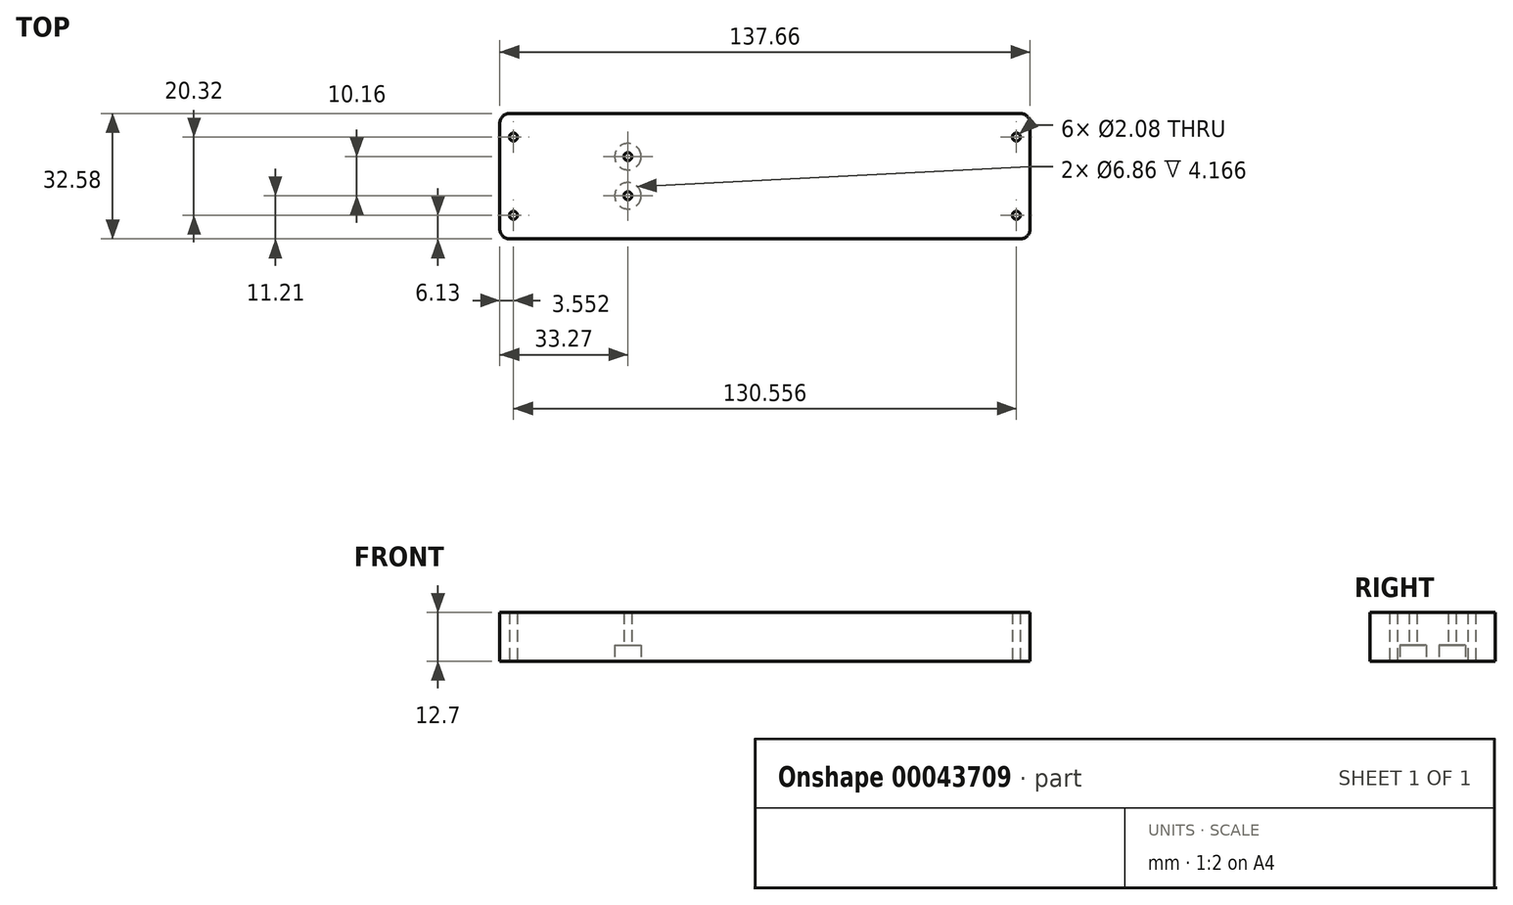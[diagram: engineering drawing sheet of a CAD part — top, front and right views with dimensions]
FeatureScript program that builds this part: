
annotation { "Feature Type Name" : "Feature", "Feature Type Description" : "" }
export const myFeature = defineFeature(function(context is Context, id is Id, definition is map)
    precondition{}
    {
        {
            var Q0;
            Q0=qCreatedBy(makeId("Top.planeOp"),FACE);
            var sketch = newSketch(context, id + "F0", { "sketchPlane" : qUnion([Q0])});
            skLineSegment(sketch, "E0.rect.bottom", {"start": v(-66.3, -16.3) * mm, "end": v(66.3, -16.3) * mm});
            skLineSegment(sketch, "E0.rect.top", {"start": v(-66.3, 16.3) * mm, "end": v(66.3, 16.3) * mm});
            skLineSegment(sketch, "E0.rect.left", {"start": v(-68.83, -13.75) * mm, "end": v(-68.83, 13.75) * mm});
            skLineSegment(sketch, "E0.rect.right", {"start": v(68.83, -13.75) * mm, "end": v(68.83, 13.75) * mm});
            skPoint(sketch, "E0.rect.middle", {"position": v(0, 0) * mm});
            skLineSegment(sketch, "E1", {"start": v(0, 16.3) * mm, "end": v(0, -16.3) * mm, "construction": true});
            skLineSegment(sketch, "E2", {"start": v(-68.83, 0) * mm, "end": v(68.83, 0) * mm, "construction": true});
            skLineSegment(sketch, "E3.rect.bottom", {"start": v(-65.28, -10.16) * mm, "end": v(65.28, -10.16) * mm, "construction": true});
            skLineSegment(sketch, "E3.rect.top", {"start": v(-65.28, 10.16) * mm, "end": v(65.28, 10.16) * mm, "construction": true});
            skLineSegment(sketch, "E3.rect.left", {"start": v(-65.28, -10.16) * mm, "end": v(-65.28, 10.16) * mm, "construction": true});
            skLineSegment(sketch, "E3.rect.right", {"start": v(65.28, -10.16) * mm, "end": v(65.28, 10.16) * mm, "construction": true});
            skCircle(sketch, "E4", {"center": v(-65.28, 10.16) * mm, "radius": 1.04 * mm});
            skCircle(sketch, "E5", {"center": v(-65.28, -10.16) * mm, "radius": 1.04 * mm});
            skCircle(sketch, "E6", {"center": v(65.28, 10.16) * mm, "radius": 1.04 * mm});
            skCircle(sketch, "E7", {"center": v(65.28, -10.16) * mm, "radius": 1.04 * mm});
            skPoint(sketch, "E8.visualSharp", {"position": v(-68.83, 16.3) * mm});
            skArc(sketch, "E8.filletArc", {"start": v(-66.3, 16.3) * mm, "mid": v(-68.1, 15.55) * mm, "end": v(-68.83, 13.75) * mm});
            skPoint(sketch, "E9.visualSharp", {"position": v(-68.83, -16.3) * mm});
            skArc(sketch, "E9.filletArc", {"start": v(-68.83, -13.75) * mm, "mid": v(-68.1, -15.55) * mm, "end": v(-66.3, -16.3) * mm});
            skPoint(sketch, "E10.visualSharp", {"position": v(68.83, 16.3) * mm});
            skArc(sketch, "E10.filletArc", {"start": v(68.83, 13.75) * mm, "mid": v(68.1, 15.55) * mm, "end": v(66.3, 16.3) * mm});
            skPoint(sketch, "E11.visualSharp", {"position": v(68.83, -16.3) * mm});
            skArc(sketch, "E11.filletArc", {"start": v(66.3, -16.3) * mm, "mid": v(68.1, -15.55) * mm, "end": v(68.83, -13.75) * mm});
            skLineSegment(sketch, "E12", {"start": v(-35.56, 16.3) * mm, "end": v(-35.56, -16.3) * mm, "construction": true});
            skSolve(sketch);
        }
        {
            var Q0;
            Q0=makeQuery(id+"F0.imprint","IMPRINT",FACE,{"disambiguationData":[TD([[makeQuery(id+"F0.imprint","IMPRINT",EDGE,{"derivedFrom":sQuery(id+"F0.wireOp",EDGE,"E0.rect.left")}),-1.0]])]});
            var Q1;
            Q1=makeQuery(id+"F0.imprint","IMPRINT",FACE,{"disambiguationData":[TD([[makeQuery(id+"F0.imprint","IMPRINT",EDGE,{"derivedFrom":sQuery(id+"F0.wireOp",EDGE,"E0.rect.right")}),1.0]])]});
            extrude(context, id + "F1", {"entities" : qUnion([Q0, Q1]), "depth" : 12.7 * mm});
        }
        {
            var Q0;
            Q0=makeQuery(id+"F1.opExtrude","CAP_FACE",FACE,{"disambiguationData":[OSD([sQuery(id+"F0.wireOp",EDGE,"E0.rect.bottom"),sQuery(id+"F0.wireOp",EDGE,"E0.rect.top"),sQuery(id+"F0.wireOp",EDGE,"E0.rect.left"),sQuery(id+"F0.wireOp",EDGE,"E0.rect.right"),sQuery(id+"F0.wireOp",EDGE,"E4"),sQuery(id+"F0.wireOp",EDGE,"E5"),sQuery(id+"F0.wireOp",EDGE,"E6"),sQuery(id+"F0.wireOp",EDGE,"E7"),sQuery(id+"F0.wireOp",EDGE,"E8.filletArc"),sQuery(id+"F0.wireOp",EDGE,"E9.filletArc"),sQuery(id+"F0.wireOp",EDGE,"E10.filletArc"),sQuery(id+"F0.wireOp",EDGE,"E11.filletArc")])],"isStart":true});
            var sketch = newSketch(context, id + "F2", { "sketchPlane" : qUnion([Q0])});
            skLineSegment(sketch, "E13", {"start": v(-68.83, 0) * mm, "end": v(0, 0) * mm, "construction": true});
            skLineSegment(sketch, "E14", {"start": v(0, 16.3) * mm, "end": v(0, -16.3) * mm, "construction": true});
            skCircle(sketch, "E15", {"center": v(-35.56, 5.08) * mm, "radius": 1.04 * mm});
            skCircle(sketch, "E16.MirrorC", {"center": v(-35.56, -5.08) * mm, "radius": 1.04 * mm});
            skSolve(sketch);
        }
        {
            var Q0;
            Q0=sQuery(id+"F2.wireOp",VERTEX,"E15.center");
            var Q1;
            Q1=sQuery(id+"F2.wireOp",VERTEX,"E16.MirrorC.center");
            var Q2;
            Q2=makeQuery(id+"F1.opExtrude","SWEPT_BODY",BODY,{"disambiguationData":[OSD([sQuery(id+"F0.wireOp",EDGE,"E0.rect.bottom"),sQuery(id+"F0.wireOp",EDGE,"E0.rect.top"),sQuery(id+"F0.wireOp",EDGE,"E0.rect.left"),sQuery(id+"F0.wireOp",EDGE,"E0.rect.right"),sQuery(id+"F0.wireOp",EDGE,"E4"),sQuery(id+"F0.wireOp",EDGE,"E5"),sQuery(id+"F0.wireOp",EDGE,"E6"),sQuery(id+"F0.wireOp",EDGE,"E7"),sQuery(id+"F0.wireOp",EDGE,"E8.filletArc"),sQuery(id+"F0.wireOp",EDGE,"E9.filletArc"),sQuery(id+"F0.wireOp",EDGE,"E10.filletArc"),sQuery(id+"F0.wireOp",EDGE,"E11.filletArc")])]});
            hole(context, id + "F3", {"style" : HoleStyle.C_BORE, "holeDiameter" : 2.08 * mm, "cBoreDiameter" : 6.86 * mm, "cBoreDepth" : 4.17 * mm, "endStyle" : HoleEndStyle.THROUGH, "locations" : qUnion([Q0, Q1]), "scope" : qUnion([Q2])});
        }
    });
